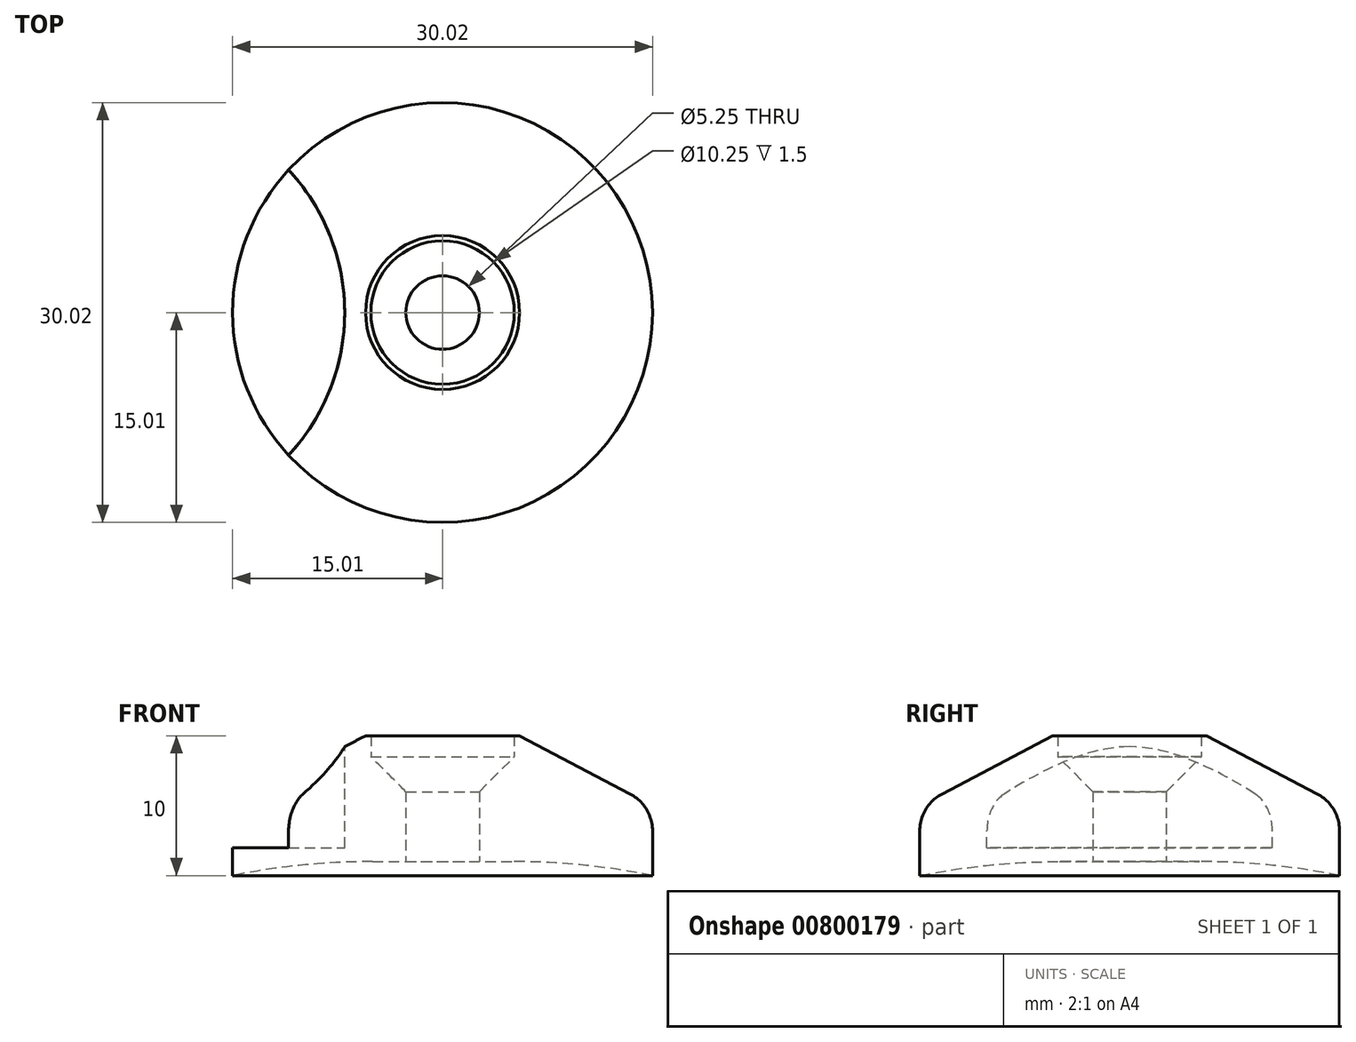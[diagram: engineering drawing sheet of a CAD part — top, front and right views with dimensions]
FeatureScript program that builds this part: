
annotation { "Feature Type Name" : "Feature", "Feature Type Description" : "" }
export const myFeature = defineFeature(function(context is Context, id is Id, definition is map)
    precondition{}
    {
        {
            var Q0;
            Q0=qCreatedBy(makeId("Front.planeOp"),FACE);
            var sketch = newSketch(context, id + "F0", { "sketchPlane" : qUnion([Q0])});
            skLineSegment(sketch, "E0.1", {"start": v(-2.63, 5) * mm, "end": v(-5.12, 7.5) * mm});
            skLineSegment(sketch, "E1.0", {"start": v(-5.12, 9) * mm, "end": v(-5.12, 7.5) * mm});
            skLineSegment(sketch, "E1.1", {"start": v(-5.12, 9) * mm, "end": v(-5.5, 9) * mm});
            skLineSegment(sketch, "E2.0", {"start": v(-5.5, 9) * mm, "end": v(-13.4, 4.84) * mm});
            skArc(sketch, "E3.0", {"start": v(-13.4, 4.84) * mm, "mid": v(-14.57, 3.74) * mm, "end": v(-15, 2.19) * mm});
            skLineSegment(sketch, "E4.0", {"start": v(-15, -1) * mm, "end": v(-15, 2.19) * mm});
            skLineSegment(sketch, "E5", {"start": v(-2.62, 0) * mm, "end": v(0, 0) * mm, "construction": true});
            skLineSegment(sketch, "E6", {"start": v(-2.63, 5) * mm, "end": v(-2.62, 0) * mm});
            skArc(sketch, "E7", {"start": v(-5, 0) * mm, "mid": v(-10.03, -0.25) * mm, "end": v(-15, -1) * mm});
            skLineSegment(sketch, "E8", {"start": v(-5, 0) * mm, "end": v(-2.62, 0) * mm});
            skLineSegment(sketch, "E9", {"start": v(0, 0) * mm, "end": v(0, 21.65) * mm, "construction": true});
            skSolve(sketch);
        }
        {
            var Q0;
            Q0=makeQuery(id+"F0.imprint","IMPRINT",FACE,{"disambiguationData":[TD([[makeQuery(id+"F0.imprint","IMPRINT",EDGE,{"derivedFrom":sQuery(id+"F0.wireOp",EDGE,"E0.1")}),1.0]])]});
            var Q1;
            Q1=sQuery(id+"F0.wireOp",EDGE,"E9");
            revolve(context, id + "F1", {"surfaceOperationType" : NewSurfaceOperationType.NEW, "entities" : qUnion([Q0]), "axis" : qUnion([Q1]), "revolveType" : RevolveType.FULL});
        }
        {
            var Q0;
            Q0=makeQuery(id+"F1.opRevolve","SWEPT_FACE",FACE,{"disambiguationData":[OSD([sQuery(id+"F0.wireOp",EDGE,"E1.1")])]});
            var sketch = newSketch(context, id + "F2", { "sketchPlane" : qUnion([Q0])});
            skCircle(sketch, "E10", {"center": v(0, 0) * mm, "radius": 5.5 * mm});
            skLineSegment(sketch, "E11", {"start": v(0, 0) * mm, "end": v(-22, 0) * mm, "construction": true});
            skCircle(sketch, "E12", {"center": v(-22, 0) * mm, "radius": 15 * mm});
            skCircle(sketch, "E13.MirrorC", {"center": v(22, 0) * mm, "radius": 15 * mm});
            skSolve(sketch);
        }
        {
            var Q0;
            Q0=makeQuery(id+"F2.imprint","IMPRINT",FACE,{"disambiguationData":[TD([[makeQuery(id+"F2.imprint","IMPRINT",EDGE,{"derivedFrom":sQuery(id+"F2.wireOp",EDGE,"E12")}),1.0]])]});
            var Q1;
            Q1=makeQuery(id+"F2.imprint","IMPRINT",FACE,{"disambiguationData":[TD([[makeQuery(id+"F2.imprint","IMPRINT",EDGE,{"derivedFrom":sQuery(id+"F2.wireOp",EDGE,"E13.MirrorC")}),-1.0]])]});
            extrude(context, id + "F3", {"entities" : qUnion([Q0, Q1]), "operationType" : NewBodyOperationType.REMOVE, "oppositeDirection" : true, "depth" : 8 * mm, "offsetDistance" : 25 * mm});
        }
    });
